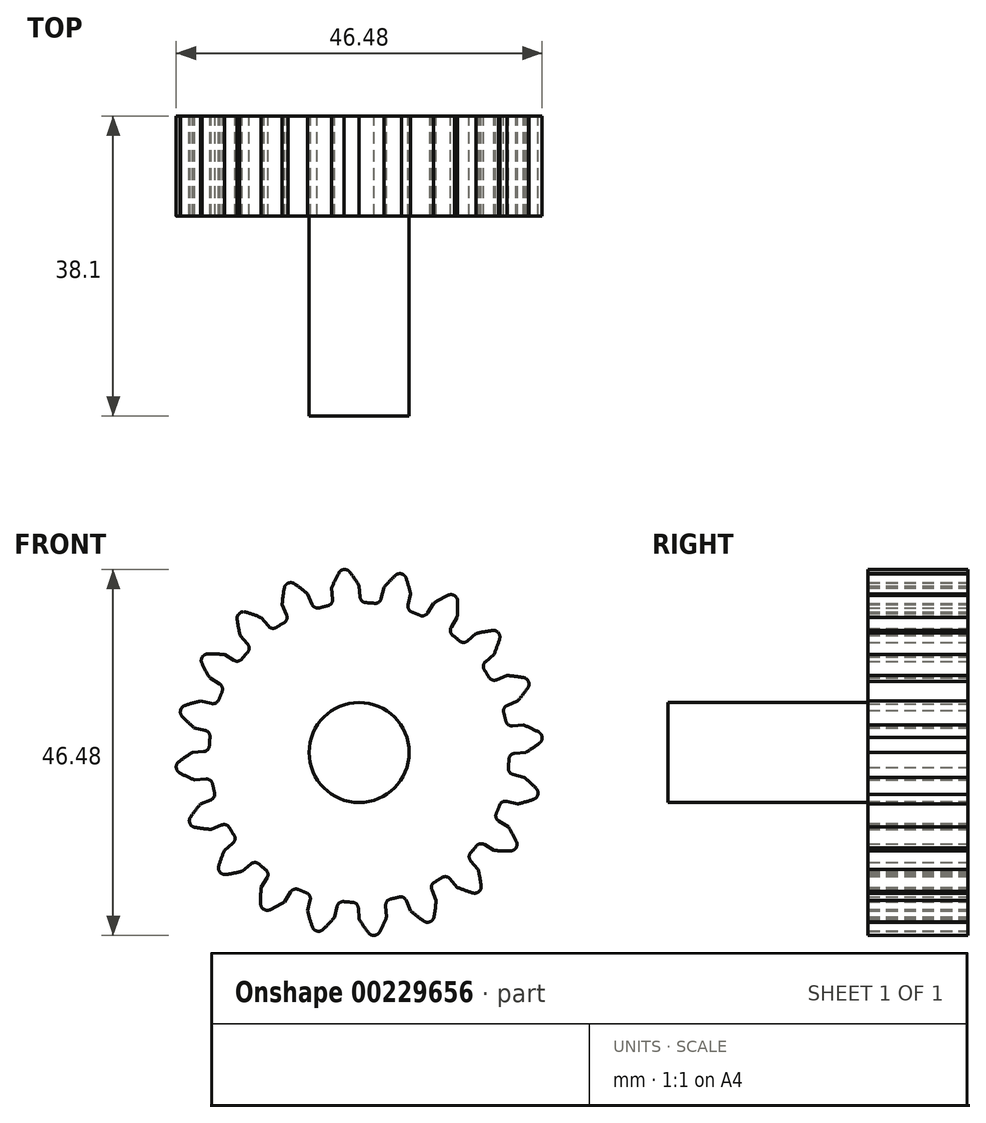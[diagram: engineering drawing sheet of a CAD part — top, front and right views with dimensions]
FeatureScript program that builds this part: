
annotation { "Feature Type Name" : "Feature", "Feature Type Description" : "" }
export const myFeature = defineFeature(function(context is Context, id is Id, definition is map)
    precondition{}
    {
        {
            var Q0;
            Q0=qCreatedBy(makeId("Front.planeOp"),FACE);
            var sketch = newSketch(context, id + "F0", { "sketchPlane" : qUnion([Q0])});
            skArc(sketch, "E0", {"start": v(-4, 18.63) * mm, "mid": v(-12.3, -14.54) * mm, "end": v(19.03, -0.86) * mm});
            skArc(sketch, "E1.trimOffspring", {"start": v(0, 21.17) * mm, "mid": v(-0.57, 22.06) * mm, "end": v(-1.2, 22.93) * mm});
            skLineSegment(sketch, "E2", {"start": v(-1.82, 23.24) * mm, "end": v(-1.92, 23.24) * mm});
            skLineSegment(sketch, "E3", {"start": v(0, 21.17) * mm, "end": v(0.11, 19.76) * mm});
            skLineSegment(sketch, "E4.MirrorCS", {"start": v(-2.01, 23.22) * mm, "end": v(-1.92, 23.24) * mm});
            skArc(sketch, "E5.MirrorCS", {"start": v(-3.49, 20.9) * mm, "mid": v(-3.06, 21.87) * mm, "end": v(-2.58, 22.82) * mm});
            skLineSegment(sketch, "E6.MirrorCS", {"start": v(-3.49, 20.9) * mm, "end": v(-3.38, 19.46) * mm});
            skPoint(sketch, "E7.visualSharp", {"position": v(0.17, 19.05) * mm});
            skArc(sketch, "E7.filletArc", {"start": v(0.11, 19.76) * mm, "mid": v(0.35, 19.25) * mm, "end": v(0.86, 19.03) * mm});
            skPoint(sketch, "E8.visualSharp", {"position": v(-3.32, 18.76) * mm});
            skArc(sketch, "E8.filletArc", {"start": v(-4, 18.63) * mm, "mid": v(-3.53, 18.93) * mm, "end": v(-3.38, 19.46) * mm});
            skPoint(sketch, "E9.visualSharp", {"position": v(-2.39, 23.16) * mm});
            skArc(sketch, "E9.filletArc", {"start": v(-2.01, 23.22) * mm, "mid": v(-2.34, 23.09) * mm, "end": v(-2.58, 22.82) * mm});
            skPoint(sketch, "E10.visualSharp", {"position": v(-1.44, 23.24) * mm});
            skArc(sketch, "E10.filletArc", {"start": v(-1.2, 22.93) * mm, "mid": v(-1.47, 23.16) * mm, "end": v(-1.82, 23.24) * mm});
            skArc(sketch, "E11.1.0", {"start": v(-9.56, 16.48) * mm, "mid": v(-9.2, 16.9) * mm, "end": v(-9.22, 17.46) * mm});
            skLineSegment(sketch, "E11.1.1", {"start": v(-9.77, 18.8) * mm, "end": v(-9.22, 17.46) * mm});
            skArc(sketch, "E11.1.2", {"start": v(-9.77, 18.8) * mm, "mid": v(-9.67, 19.85) * mm, "end": v(-9.5, 20.9) * mm});
            skArc(sketch, "E11.1.3", {"start": v(-9.09, 21.47) * mm, "mid": v(-9.36, 21.24) * mm, "end": v(-9.5, 20.9) * mm});
            skLineSegment(sketch, "E11.1.4", {"start": v(-9.09, 21.47) * mm, "end": v(-9, 21.5) * mm});
            skLineSegment(sketch, "E11.1.5", {"start": v(-8.92, 21.54) * mm, "end": v(-9, 21.5) * mm});
            skArc(sketch, "E11.1.6", {"start": v(-8.23, 21.44) * mm, "mid": v(-8.56, 21.57) * mm, "end": v(-8.92, 21.54) * mm});
            skArc(sketch, "E11.1.7", {"start": v(-6.54, 20.13) * mm, "mid": v(-7.36, 20.8) * mm, "end": v(-8.23, 21.44) * mm});
            skLineSegment(sketch, "E11.1.8", {"start": v(-6.54, 20.13) * mm, "end": v(-6, 18.82) * mm});
            skArc(sketch, "E11.1.9", {"start": v(-6, 18.82) * mm, "mid": v(-5.62, 18.42) * mm, "end": v(-5.06, 18.37) * mm});
            skArc(sketch, "E11.2.0", {"start": v(-14.18, 12.72) * mm, "mid": v(-13.98, 13.24) * mm, "end": v(-14.17, 13.76) * mm});
            skLineSegment(sketch, "E11.2.1", {"start": v(-15.1, 14.85) * mm, "end": v(-14.17, 13.76) * mm});
            skArc(sketch, "E11.2.2", {"start": v(-15.1, 14.85) * mm, "mid": v(-15.33, 15.9) * mm, "end": v(-15.5, 16.95) * mm});
            skArc(sketch, "E11.2.3", {"start": v(-15.28, 17.6) * mm, "mid": v(-15.47, 17.3) * mm, "end": v(-15.5, 16.95) * mm});
            skLineSegment(sketch, "E11.2.4", {"start": v(-15.28, 17.6) * mm, "end": v(-15.21, 17.67) * mm});
            skLineSegment(sketch, "E11.2.5", {"start": v(-15.13, 17.73) * mm, "end": v(-15.21, 17.67) * mm});
            skArc(sketch, "E11.2.6", {"start": v(-14.45, 17.85) * mm, "mid": v(-14.8, 17.87) * mm, "end": v(-15.13, 17.73) * mm});
            skArc(sketch, "E11.2.7", {"start": v(-12.44, 17.12) * mm, "mid": v(-13.43, 17.51) * mm, "end": v(-14.45, 17.85) * mm});
            skLineSegment(sketch, "E11.2.8", {"start": v(-12.44, 17.12) * mm, "end": v(-11.52, 16.05) * mm});
            skArc(sketch, "E11.2.9", {"start": v(-11.52, 16.05) * mm, "mid": v(-11.03, 15.78) * mm, "end": v(-10.49, 15.9) * mm});
            skArc(sketch, "E11.3.0", {"start": v(-17.42, 7.72) * mm, "mid": v(-17.39, 8.27) * mm, "end": v(-17.73, 8.7) * mm});
            skLineSegment(sketch, "E11.3.1", {"start": v(-18.95, 9.46) * mm, "end": v(-17.73, 8.7) * mm});
            skArc(sketch, "E11.3.2", {"start": v(-18.95, 9.46) * mm, "mid": v(-19.5, 10.38) * mm, "end": v(-19.98, 11.33) * mm});
            skArc(sketch, "E11.3.3", {"start": v(-19.97, 12.02) * mm, "mid": v(-20.06, 11.68) * mm, "end": v(-19.98, 11.33) * mm});
            skLineSegment(sketch, "E11.3.4", {"start": v(-19.97, 12.02) * mm, "end": v(-19.93, 12.1) * mm});
            skLineSegment(sketch, "E11.3.5", {"start": v(-19.87, 12.18) * mm, "end": v(-19.93, 12.1) * mm});
            skArc(sketch, "E11.3.6", {"start": v(-19.25, 12.5) * mm, "mid": v(-19.6, 12.42) * mm, "end": v(-19.87, 12.18) * mm});
            skArc(sketch, "E11.3.7", {"start": v(-17.12, 12.44) * mm, "mid": v(-18.19, 12.5) * mm, "end": v(-19.25, 12.5) * mm});
            skLineSegment(sketch, "E11.3.8", {"start": v(-17.12, 12.44) * mm, "end": v(-15.92, 11.7) * mm});
            skArc(sketch, "E11.3.9", {"start": v(-15.92, 11.7) * mm, "mid": v(-15.37, 11.6) * mm, "end": v(-14.9, 11.88) * mm});
            skArc(sketch, "E11.4.0", {"start": v(-18.95, 1.96) * mm, "mid": v(-19.09, 2.5) * mm, "end": v(-19.55, 2.8) * mm});
            skLineSegment(sketch, "E11.4.1", {"start": v(-20.95, 3.14) * mm, "end": v(-19.55, 2.8) * mm});
            skArc(sketch, "E11.4.2", {"start": v(-20.95, 3.14) * mm, "mid": v(-21.74, 3.85) * mm, "end": v(-22.5, 4.6) * mm});
            skArc(sketch, "E11.4.3", {"start": v(-22.7, 5.26) * mm, "mid": v(-22.68, 4.9) * mm, "end": v(-22.5, 4.6) * mm});
            skLineSegment(sketch, "E11.4.4", {"start": v(-22.7, 5.26) * mm, "end": v(-22.7, 5.36) * mm});
            skLineSegment(sketch, "E11.4.5", {"start": v(-22.66, 5.45) * mm, "end": v(-22.7, 5.36) * mm});
            skArc(sketch, "E11.4.6", {"start": v(-22.18, 5.95) * mm, "mid": v(-22.48, 5.75) * mm, "end": v(-22.66, 5.45) * mm});
            skArc(sketch, "E11.4.7", {"start": v(-20.13, 6.54) * mm, "mid": v(-21.16, 6.27) * mm, "end": v(-22.18, 5.95) * mm});
            skLineSegment(sketch, "E11.4.8", {"start": v(-20.13, 6.54) * mm, "end": v(-18.75, 6.21) * mm});
            skArc(sketch, "E11.4.9", {"start": v(-18.75, 6.21) * mm, "mid": v(-18.2, 6.28) * mm, "end": v(-17.83, 6.7) * mm});
            skArc(sketch, "E11.5.0", {"start": v(-18.63, -4) * mm, "mid": v(-18.93, -3.53) * mm, "end": v(-19.46, -3.38) * mm});
            skLineSegment(sketch, "E11.5.1", {"start": v(-20.9, -3.49) * mm, "end": v(-19.46, -3.38) * mm});
            skArc(sketch, "E11.5.2", {"start": v(-20.9, -3.49) * mm, "mid": v(-21.87, -3.06) * mm, "end": v(-22.82, -2.58) * mm});
            skArc(sketch, "E11.5.3", {"start": v(-23.22, -2.01) * mm, "mid": v(-23.09, -2.34) * mm, "end": v(-22.82, -2.58) * mm});
            skLineSegment(sketch, "E11.5.4", {"start": v(-23.22, -2.01) * mm, "end": v(-23.24, -1.92) * mm});
            skLineSegment(sketch, "E11.5.5", {"start": v(-23.24, -1.82) * mm, "end": v(-23.24, -1.92) * mm});
            skArc(sketch, "E11.5.6", {"start": v(-22.93, -1.2) * mm, "mid": v(-23.16, -1.47) * mm, "end": v(-23.24, -1.82) * mm});
            skArc(sketch, "E11.5.7", {"start": v(-21.17, 0) * mm, "mid": v(-22.06, -0.57) * mm, "end": v(-22.93, -1.2) * mm});
            skLineSegment(sketch, "E11.5.8", {"start": v(-21.17, 0) * mm, "end": v(-19.76, 0.11) * mm});
            skArc(sketch, "E11.5.9", {"start": v(-19.76, 0.11) * mm, "mid": v(-19.25, 0.35) * mm, "end": v(-19.03, 0.86) * mm});
            skArc(sketch, "E11.6.0", {"start": v(-16.48, -9.56) * mm, "mid": v(-16.9, -9.2) * mm, "end": v(-17.46, -9.22) * mm});
            skLineSegment(sketch, "E11.6.1", {"start": v(-18.8, -9.77) * mm, "end": v(-17.46, -9.22) * mm});
            skArc(sketch, "E11.6.2", {"start": v(-18.8, -9.77) * mm, "mid": v(-19.85, -9.67) * mm, "end": v(-20.9, -9.5) * mm});
            skArc(sketch, "E11.6.3", {"start": v(-21.47, -9.09) * mm, "mid": v(-21.24, -9.36) * mm, "end": v(-20.9, -9.5) * mm});
            skLineSegment(sketch, "E11.6.4", {"start": v(-21.47, -9.09) * mm, "end": v(-21.5, -9) * mm});
            skLineSegment(sketch, "E11.6.5", {"start": v(-21.54, -8.92) * mm, "end": v(-21.5, -9) * mm});
            skArc(sketch, "E11.6.6", {"start": v(-21.44, -8.23) * mm, "mid": v(-21.57, -8.56) * mm, "end": v(-21.54, -8.92) * mm});
            skArc(sketch, "E11.6.7", {"start": v(-20.13, -6.54) * mm, "mid": v(-20.8, -7.36) * mm, "end": v(-21.44, -8.23) * mm});
            skLineSegment(sketch, "E11.6.8", {"start": v(-20.13, -6.54) * mm, "end": v(-18.82, -6) * mm});
            skArc(sketch, "E11.6.9", {"start": v(-18.82, -6) * mm, "mid": v(-18.42, -5.62) * mm, "end": v(-18.37, -5.06) * mm});
            skArc(sketch, "E11.7.0", {"start": v(-12.72, -14.18) * mm, "mid": v(-13.24, -13.98) * mm, "end": v(-13.76, -14.17) * mm});
            skLineSegment(sketch, "E11.7.1", {"start": v(-14.85, -15.1) * mm, "end": v(-13.76, -14.17) * mm});
            skArc(sketch, "E11.7.2", {"start": v(-14.85, -15.1) * mm, "mid": v(-15.9, -15.33) * mm, "end": v(-16.95, -15.5) * mm});
            skArc(sketch, "E11.7.3", {"start": v(-17.6, -15.28) * mm, "mid": v(-17.3, -15.47) * mm, "end": v(-16.95, -15.5) * mm});
            skLineSegment(sketch, "E11.7.4", {"start": v(-17.6, -15.28) * mm, "end": v(-17.67, -15.21) * mm});
            skLineSegment(sketch, "E11.7.5", {"start": v(-17.73, -15.13) * mm, "end": v(-17.67, -15.21) * mm});
            skArc(sketch, "E11.7.6", {"start": v(-17.85, -14.45) * mm, "mid": v(-17.87, -14.8) * mm, "end": v(-17.73, -15.13) * mm});
            skArc(sketch, "E11.7.7", {"start": v(-17.12, -12.44) * mm, "mid": v(-17.51, -13.43) * mm, "end": v(-17.85, -14.45) * mm});
            skLineSegment(sketch, "E11.7.8", {"start": v(-17.12, -12.44) * mm, "end": v(-16.05, -11.52) * mm});
            skArc(sketch, "E11.7.9", {"start": v(-16.05, -11.52) * mm, "mid": v(-15.78, -11.03) * mm, "end": v(-15.9, -10.49) * mm});
            skArc(sketch, "E11.8.0", {"start": v(-7.72, -17.42) * mm, "mid": v(-8.27, -17.39) * mm, "end": v(-8.7, -17.73) * mm});
            skLineSegment(sketch, "E11.8.1", {"start": v(-9.46, -18.95) * mm, "end": v(-8.7, -17.73) * mm});
            skArc(sketch, "E11.8.2", {"start": v(-9.46, -18.95) * mm, "mid": v(-10.38, -19.5) * mm, "end": v(-11.33, -19.98) * mm});
            skArc(sketch, "E11.8.3", {"start": v(-12.02, -19.97) * mm, "mid": v(-11.68, -20.06) * mm, "end": v(-11.33, -19.98) * mm});
            skLineSegment(sketch, "E11.8.4", {"start": v(-12.02, -19.97) * mm, "end": v(-12.1, -19.93) * mm});
            skLineSegment(sketch, "E11.8.5", {"start": v(-12.18, -19.87) * mm, "end": v(-12.1, -19.93) * mm});
            skArc(sketch, "E11.8.6", {"start": v(-12.5, -19.25) * mm, "mid": v(-12.42, -19.6) * mm, "end": v(-12.18, -19.87) * mm});
            skArc(sketch, "E11.8.7", {"start": v(-12.44, -17.12) * mm, "mid": v(-12.5, -18.19) * mm, "end": v(-12.5, -19.25) * mm});
            skLineSegment(sketch, "E11.8.8", {"start": v(-12.44, -17.12) * mm, "end": v(-11.7, -15.92) * mm});
            skArc(sketch, "E11.8.9", {"start": v(-11.7, -15.92) * mm, "mid": v(-11.6, -15.37) * mm, "end": v(-11.88, -14.9) * mm});
            skArc(sketch, "E11.9.0", {"start": v(-1.96, -18.95) * mm, "mid": v(-2.5, -19.09) * mm, "end": v(-2.8, -19.55) * mm});
            skLineSegment(sketch, "E11.9.1", {"start": v(-3.14, -20.95) * mm, "end": v(-2.8, -19.55) * mm});
            skArc(sketch, "E11.9.2", {"start": v(-3.14, -20.95) * mm, "mid": v(-3.85, -21.74) * mm, "end": v(-4.6, -22.5) * mm});
            skArc(sketch, "E11.9.3", {"start": v(-5.26, -22.7) * mm, "mid": v(-4.9, -22.68) * mm, "end": v(-4.6, -22.5) * mm});
            skLineSegment(sketch, "E11.9.4", {"start": v(-5.26, -22.7) * mm, "end": v(-5.36, -22.7) * mm});
            skLineSegment(sketch, "E11.9.5", {"start": v(-5.45, -22.66) * mm, "end": v(-5.36, -22.7) * mm});
            skArc(sketch, "E11.9.6", {"start": v(-5.95, -22.18) * mm, "mid": v(-5.75, -22.48) * mm, "end": v(-5.45, -22.66) * mm});
            skArc(sketch, "E11.9.7", {"start": v(-6.54, -20.13) * mm, "mid": v(-6.27, -21.16) * mm, "end": v(-5.95, -22.18) * mm});
            skLineSegment(sketch, "E11.9.8", {"start": v(-6.54, -20.13) * mm, "end": v(-6.21, -18.75) * mm});
            skArc(sketch, "E11.9.9", {"start": v(-6.21, -18.75) * mm, "mid": v(-6.28, -18.2) * mm, "end": v(-6.7, -17.83) * mm});
            skArc(sketch, "E11.10.0", {"start": v(4, -18.63) * mm, "mid": v(3.53, -18.93) * mm, "end": v(3.38, -19.46) * mm});
            skLineSegment(sketch, "E11.10.1", {"start": v(3.49, -20.9) * mm, "end": v(3.38, -19.46) * mm});
            skArc(sketch, "E11.10.2", {"start": v(3.49, -20.9) * mm, "mid": v(3.06, -21.87) * mm, "end": v(2.58, -22.82) * mm});
            skArc(sketch, "E11.10.3", {"start": v(2.01, -23.22) * mm, "mid": v(2.34, -23.09) * mm, "end": v(2.58, -22.82) * mm});
            skLineSegment(sketch, "E11.10.4", {"start": v(2.01, -23.22) * mm, "end": v(1.92, -23.24) * mm});
            skLineSegment(sketch, "E11.10.5", {"start": v(1.82, -23.24) * mm, "end": v(1.92, -23.24) * mm});
            skArc(sketch, "E11.10.6", {"start": v(1.2, -22.93) * mm, "mid": v(1.47, -23.16) * mm, "end": v(1.82, -23.24) * mm});
            skArc(sketch, "E11.10.7", {"start": v(0, -21.17) * mm, "mid": v(0.57, -22.06) * mm, "end": v(1.2, -22.93) * mm});
            skLineSegment(sketch, "E11.10.8", {"start": v(0, -21.17) * mm, "end": v(-0.11, -19.76) * mm});
            skArc(sketch, "E11.10.9", {"start": v(-0.11, -19.76) * mm, "mid": v(-0.35, -19.25) * mm, "end": v(-0.86, -19.03) * mm});
            skArc(sketch, "E11.11.0", {"start": v(9.56, -16.48) * mm, "mid": v(9.2, -16.9) * mm, "end": v(9.22, -17.46) * mm});
            skLineSegment(sketch, "E11.11.1", {"start": v(9.77, -18.8) * mm, "end": v(9.22, -17.46) * mm});
            skArc(sketch, "E11.11.2", {"start": v(9.77, -18.8) * mm, "mid": v(9.67, -19.85) * mm, "end": v(9.5, -20.9) * mm});
            skArc(sketch, "E11.11.3", {"start": v(9.09, -21.47) * mm, "mid": v(9.36, -21.24) * mm, "end": v(9.5, -20.9) * mm});
            skLineSegment(sketch, "E11.11.4", {"start": v(9.09, -21.47) * mm, "end": v(9, -21.5) * mm});
            skLineSegment(sketch, "E11.11.5", {"start": v(8.92, -21.54) * mm, "end": v(9, -21.5) * mm});
            skArc(sketch, "E11.11.6", {"start": v(8.23, -21.44) * mm, "mid": v(8.56, -21.57) * mm, "end": v(8.92, -21.54) * mm});
            skArc(sketch, "E11.11.7", {"start": v(6.54, -20.13) * mm, "mid": v(7.36, -20.8) * mm, "end": v(8.23, -21.44) * mm});
            skLineSegment(sketch, "E11.11.8", {"start": v(6.54, -20.13) * mm, "end": v(6, -18.82) * mm});
            skArc(sketch, "E11.11.9", {"start": v(6, -18.82) * mm, "mid": v(5.62, -18.42) * mm, "end": v(5.06, -18.37) * mm});
            skArc(sketch, "E11.12.0", {"start": v(14.18, -12.72) * mm, "mid": v(13.98, -13.24) * mm, "end": v(14.17, -13.76) * mm});
            skLineSegment(sketch, "E11.12.1", {"start": v(15.1, -14.85) * mm, "end": v(14.17, -13.76) * mm});
            skArc(sketch, "E11.12.2", {"start": v(15.1, -14.85) * mm, "mid": v(15.33, -15.9) * mm, "end": v(15.5, -16.95) * mm});
            skArc(sketch, "E11.12.3", {"start": v(15.28, -17.6) * mm, "mid": v(15.47, -17.3) * mm, "end": v(15.5, -16.95) * mm});
            skLineSegment(sketch, "E11.12.4", {"start": v(15.28, -17.6) * mm, "end": v(15.21, -17.67) * mm});
            skLineSegment(sketch, "E11.12.5", {"start": v(15.13, -17.73) * mm, "end": v(15.21, -17.67) * mm});
            skArc(sketch, "E11.12.6", {"start": v(14.45, -17.85) * mm, "mid": v(14.8, -17.87) * mm, "end": v(15.13, -17.73) * mm});
            skArc(sketch, "E11.12.7", {"start": v(12.44, -17.12) * mm, "mid": v(13.43, -17.51) * mm, "end": v(14.45, -17.85) * mm});
            skLineSegment(sketch, "E11.12.8", {"start": v(12.44, -17.12) * mm, "end": v(11.52, -16.05) * mm});
            skArc(sketch, "E11.12.9", {"start": v(11.52, -16.05) * mm, "mid": v(11.03, -15.78) * mm, "end": v(10.49, -15.9) * mm});
            skArc(sketch, "E11.13.0", {"start": v(17.42, -7.72) * mm, "mid": v(17.39, -8.27) * mm, "end": v(17.73, -8.7) * mm});
            skLineSegment(sketch, "E11.13.1", {"start": v(18.95, -9.46) * mm, "end": v(17.73, -8.7) * mm});
            skArc(sketch, "E11.13.2", {"start": v(18.95, -9.46) * mm, "mid": v(19.5, -10.38) * mm, "end": v(19.98, -11.33) * mm});
            skArc(sketch, "E11.13.3", {"start": v(19.97, -12.02) * mm, "mid": v(20.06, -11.68) * mm, "end": v(19.98, -11.33) * mm});
            skLineSegment(sketch, "E11.13.4", {"start": v(19.97, -12.02) * mm, "end": v(19.93, -12.1) * mm});
            skLineSegment(sketch, "E11.13.5", {"start": v(19.87, -12.18) * mm, "end": v(19.93, -12.1) * mm});
            skArc(sketch, "E11.13.6", {"start": v(19.25, -12.5) * mm, "mid": v(19.6, -12.42) * mm, "end": v(19.87, -12.18) * mm});
            skArc(sketch, "E11.13.7", {"start": v(17.12, -12.44) * mm, "mid": v(18.19, -12.5) * mm, "end": v(19.25, -12.5) * mm});
            skLineSegment(sketch, "E11.13.8", {"start": v(17.12, -12.44) * mm, "end": v(15.92, -11.7) * mm});
            skArc(sketch, "E11.13.9", {"start": v(15.92, -11.7) * mm, "mid": v(15.37, -11.6) * mm, "end": v(14.9, -11.88) * mm});
            skArc(sketch, "E11.14.0", {"start": v(18.95, -1.96) * mm, "mid": v(19.09, -2.5) * mm, "end": v(19.55, -2.8) * mm});
            skLineSegment(sketch, "E11.14.1", {"start": v(20.95, -3.14) * mm, "end": v(19.55, -2.8) * mm});
            skArc(sketch, "E11.14.2", {"start": v(20.95, -3.14) * mm, "mid": v(21.74, -3.85) * mm, "end": v(22.5, -4.6) * mm});
            skArc(sketch, "E11.14.3", {"start": v(22.7, -5.26) * mm, "mid": v(22.68, -4.9) * mm, "end": v(22.5, -4.6) * mm});
            skLineSegment(sketch, "E11.14.4", {"start": v(22.7, -5.26) * mm, "end": v(22.7, -5.36) * mm});
            skLineSegment(sketch, "E11.14.5", {"start": v(22.66, -5.45) * mm, "end": v(22.7, -5.36) * mm});
            skArc(sketch, "E11.14.6", {"start": v(22.18, -5.95) * mm, "mid": v(22.48, -5.75) * mm, "end": v(22.66, -5.45) * mm});
            skArc(sketch, "E11.14.7", {"start": v(20.13, -6.54) * mm, "mid": v(21.16, -6.27) * mm, "end": v(22.18, -5.95) * mm});
            skLineSegment(sketch, "E11.14.8", {"start": v(20.13, -6.54) * mm, "end": v(18.75, -6.21) * mm});
            skArc(sketch, "E11.14.9", {"start": v(18.75, -6.21) * mm, "mid": v(18.2, -6.28) * mm, "end": v(17.83, -6.7) * mm});
            skArc(sketch, "E11.15.0", {"start": v(18.63, 4) * mm, "mid": v(18.93, 3.53) * mm, "end": v(19.46, 3.38) * mm});
            skLineSegment(sketch, "E11.15.1", {"start": v(20.9, 3.49) * mm, "end": v(19.46, 3.38) * mm});
            skArc(sketch, "E11.15.2", {"start": v(20.9, 3.49) * mm, "mid": v(21.87, 3.06) * mm, "end": v(22.82, 2.58) * mm});
            skArc(sketch, "E11.15.3", {"start": v(23.22, 2.01) * mm, "mid": v(23.09, 2.34) * mm, "end": v(22.82, 2.58) * mm});
            skLineSegment(sketch, "E11.15.4", {"start": v(23.22, 2.01) * mm, "end": v(23.24, 1.92) * mm});
            skLineSegment(sketch, "E11.15.5", {"start": v(23.24, 1.82) * mm, "end": v(23.24, 1.92) * mm});
            skArc(sketch, "E11.15.6", {"start": v(22.93, 1.2) * mm, "mid": v(23.16, 1.47) * mm, "end": v(23.24, 1.82) * mm});
            skArc(sketch, "E11.15.7", {"start": v(21.17, 0) * mm, "mid": v(22.06, 0.57) * mm, "end": v(22.93, 1.2) * mm});
            skLineSegment(sketch, "E11.15.8", {"start": v(21.17, 0) * mm, "end": v(19.76, -0.11) * mm});
            skArc(sketch, "E11.15.9", {"start": v(19.76, -0.11) * mm, "mid": v(19.25, -0.35) * mm, "end": v(19.03, -0.86) * mm});
            skArc(sketch, "E11.16.0", {"start": v(16.48, 9.56) * mm, "mid": v(16.9, 9.2) * mm, "end": v(17.46, 9.22) * mm});
            skLineSegment(sketch, "E11.16.1", {"start": v(18.8, 9.77) * mm, "end": v(17.46, 9.22) * mm});
            skArc(sketch, "E11.16.2", {"start": v(18.8, 9.77) * mm, "mid": v(19.85, 9.67) * mm, "end": v(20.9, 9.5) * mm});
            skArc(sketch, "E11.16.3", {"start": v(21.47, 9.09) * mm, "mid": v(21.24, 9.36) * mm, "end": v(20.9, 9.5) * mm});
            skLineSegment(sketch, "E11.16.4", {"start": v(21.47, 9.09) * mm, "end": v(21.5, 9) * mm});
            skLineSegment(sketch, "E11.16.5", {"start": v(21.54, 8.92) * mm, "end": v(21.5, 9) * mm});
            skArc(sketch, "E11.16.6", {"start": v(21.44, 8.23) * mm, "mid": v(21.57, 8.56) * mm, "end": v(21.54, 8.92) * mm});
            skArc(sketch, "E11.16.7", {"start": v(20.13, 6.54) * mm, "mid": v(20.8, 7.36) * mm, "end": v(21.44, 8.23) * mm});
            skLineSegment(sketch, "E11.16.8", {"start": v(20.13, 6.54) * mm, "end": v(18.82, 6) * mm});
            skArc(sketch, "E11.16.9", {"start": v(18.82, 6) * mm, "mid": v(18.42, 5.62) * mm, "end": v(18.37, 5.06) * mm});
            skArc(sketch, "E11.17.0", {"start": v(12.72, 14.18) * mm, "mid": v(13.24, 13.98) * mm, "end": v(13.76, 14.17) * mm});
            skLineSegment(sketch, "E11.17.1", {"start": v(14.85, 15.1) * mm, "end": v(13.76, 14.17) * mm});
            skArc(sketch, "E11.17.2", {"start": v(14.85, 15.1) * mm, "mid": v(15.9, 15.33) * mm, "end": v(16.95, 15.5) * mm});
            skArc(sketch, "E11.17.3", {"start": v(17.6, 15.28) * mm, "mid": v(17.3, 15.47) * mm, "end": v(16.95, 15.5) * mm});
            skLineSegment(sketch, "E11.17.4", {"start": v(17.6, 15.28) * mm, "end": v(17.67, 15.21) * mm});
            skLineSegment(sketch, "E11.17.5", {"start": v(17.73, 15.13) * mm, "end": v(17.67, 15.21) * mm});
            skArc(sketch, "E11.17.6", {"start": v(17.85, 14.45) * mm, "mid": v(17.87, 14.8) * mm, "end": v(17.73, 15.13) * mm});
            skArc(sketch, "E11.17.7", {"start": v(17.12, 12.44) * mm, "mid": v(17.51, 13.43) * mm, "end": v(17.85, 14.45) * mm});
            skLineSegment(sketch, "E11.17.8", {"start": v(17.12, 12.44) * mm, "end": v(16.05, 11.52) * mm});
            skArc(sketch, "E11.17.9", {"start": v(16.05, 11.52) * mm, "mid": v(15.78, 11.03) * mm, "end": v(15.9, 10.49) * mm});
            skArc(sketch, "E11.18.0", {"start": v(7.72, 17.42) * mm, "mid": v(8.27, 17.39) * mm, "end": v(8.7, 17.73) * mm});
            skLineSegment(sketch, "E11.18.1", {"start": v(9.46, 18.95) * mm, "end": v(8.7, 17.73) * mm});
            skArc(sketch, "E11.18.2", {"start": v(9.46, 18.95) * mm, "mid": v(10.38, 19.5) * mm, "end": v(11.33, 19.98) * mm});
            skArc(sketch, "E11.18.3", {"start": v(12.02, 19.97) * mm, "mid": v(11.68, 20.06) * mm, "end": v(11.33, 19.98) * mm});
            skLineSegment(sketch, "E11.18.4", {"start": v(12.02, 19.97) * mm, "end": v(12.1, 19.93) * mm});
            skLineSegment(sketch, "E11.18.5", {"start": v(12.18, 19.87) * mm, "end": v(12.1, 19.93) * mm});
            skArc(sketch, "E11.18.6", {"start": v(12.5, 19.25) * mm, "mid": v(12.42, 19.6) * mm, "end": v(12.18, 19.87) * mm});
            skArc(sketch, "E11.18.7", {"start": v(12.44, 17.12) * mm, "mid": v(12.5, 18.19) * mm, "end": v(12.5, 19.25) * mm});
            skLineSegment(sketch, "E11.18.8", {"start": v(12.44, 17.12) * mm, "end": v(11.7, 15.92) * mm});
            skArc(sketch, "E11.18.9", {"start": v(11.7, 15.92) * mm, "mid": v(11.6, 15.37) * mm, "end": v(11.88, 14.9) * mm});
            skArc(sketch, "E11.19.0", {"start": v(1.96, 18.95) * mm, "mid": v(2.5, 19.09) * mm, "end": v(2.8, 19.55) * mm});
            skLineSegment(sketch, "E11.19.1", {"start": v(3.14, 20.95) * mm, "end": v(2.8, 19.55) * mm});
            skArc(sketch, "E11.19.2", {"start": v(3.14, 20.95) * mm, "mid": v(3.85, 21.74) * mm, "end": v(4.6, 22.5) * mm});
            skArc(sketch, "E11.19.3", {"start": v(5.26, 22.7) * mm, "mid": v(4.9, 22.68) * mm, "end": v(4.6, 22.5) * mm});
            skLineSegment(sketch, "E11.19.4", {"start": v(5.26, 22.7) * mm, "end": v(5.36, 22.7) * mm});
            skLineSegment(sketch, "E11.19.5", {"start": v(5.45, 22.66) * mm, "end": v(5.36, 22.7) * mm});
            skArc(sketch, "E11.19.6", {"start": v(5.95, 22.18) * mm, "mid": v(5.75, 22.48) * mm, "end": v(5.45, 22.66) * mm});
            skArc(sketch, "E11.19.7", {"start": v(6.54, 20.13) * mm, "mid": v(6.27, 21.16) * mm, "end": v(5.95, 22.18) * mm});
            skLineSegment(sketch, "E11.19.8", {"start": v(6.54, 20.13) * mm, "end": v(6.21, 18.75) * mm});
            skArc(sketch, "E11.19.9", {"start": v(6.21, 18.75) * mm, "mid": v(6.28, 18.2) * mm, "end": v(6.7, 17.83) * mm});
            skArc(sketch, "E12.trimOffspring", {"start": v(1.96, 18.95) * mm, "mid": v(1.4, 19) * mm, "end": v(0.86, 19.03) * mm});
            skArc(sketch, "E13.trimOffspring", {"start": v(7.72, 17.42) * mm, "mid": v(7.21, 17.63) * mm, "end": v(6.7, 17.83) * mm});
            skArc(sketch, "E14.trimOffspring", {"start": v(12.72, 14.18) * mm, "mid": v(12.3, 14.54) * mm, "end": v(11.88, 14.9) * mm});
            skArc(sketch, "E15.trimOffspring", {"start": v(16.48, 9.56) * mm, "mid": v(16.2, 10.03) * mm, "end": v(15.9, 10.49) * mm});
            skArc(sketch, "E16.trimOffspring", {"start": v(18.63, 4) * mm, "mid": v(18.5, 4.53) * mm, "end": v(18.37, 5.06) * mm});
            skSolve(sketch);
        }
        {
            var Q0;
            Q0=qSketchRegion(id+"F0",true);
            extrude(context, id + "F1", {"entities" : qUnion([Q0]), "depth" : 12.7 * mm});
        }
        {
            var Q0;
            Q0=makeQuery(id+"F1.opExtrude","CAP_FACE",FACE,{"disambiguationData":[OSD([sQuery(id+"F0.wireOp",EDGE,"E0"),sQuery(id+"F0.wireOp",EDGE,"E1.trimOffspring"),sQuery(id+"F0.wireOp",EDGE,"E2"),sQuery(id+"F0.wireOp",EDGE,"E3"),sQuery(id+"F0.wireOp",EDGE,"E4.MirrorCS"),sQuery(id+"F0.wireOp",EDGE,"E5.MirrorCS"),sQuery(id+"F0.wireOp",EDGE,"E6.MirrorCS"),sQuery(id+"F0.wireOp",EDGE,"E7.filletArc"),sQuery(id+"F0.wireOp",EDGE,"E8.filletArc"),sQuery(id+"F0.wireOp",EDGE,"E9.filletArc"),sQuery(id+"F0.wireOp",EDGE,"E10.filletArc"),sQuery(id+"F0.wireOp",EDGE,"E11.1.0"),sQuery(id+"F0.wireOp",EDGE,"E11.1.1"),sQuery(id+"F0.wireOp",EDGE,"E11.1.2"),sQuery(id+"F0.wireOp",EDGE,"E11.1.3"),sQuery(id+"F0.wireOp",EDGE,"E11.1.4"),sQuery(id+"F0.wireOp",EDGE,"E11.1.5"),sQuery(id+"F0.wireOp",EDGE,"E11.1.6"),sQuery(id+"F0.wireOp",EDGE,"E11.1.7"),sQuery(id+"F0.wireOp",EDGE,"E11.1.8"),sQuery(id+"F0.wireOp",EDGE,"E11.1.9"),sQuery(id+"F0.wireOp",EDGE,"E11.2.0"),sQuery(id+"F0.wireOp",EDGE,"E11.2.1"),sQuery(id+"F0.wireOp",EDGE,"E11.2.2"),sQuery(id+"F0.wireOp",EDGE,"E11.2.3"),sQuery(id+"F0.wireOp",EDGE,"E11.2.4"),sQuery(id+"F0.wireOp",EDGE,"E11.2.5"),sQuery(id+"F0.wireOp",EDGE,"E11.2.6"),sQuery(id+"F0.wireOp",EDGE,"E11.2.7"),sQuery(id+"F0.wireOp",EDGE,"E11.2.8"),sQuery(id+"F0.wireOp",EDGE,"E11.2.9"),sQuery(id+"F0.wireOp",EDGE,"E11.3.0"),sQuery(id+"F0.wireOp",EDGE,"E11.3.1"),sQuery(id+"F0.wireOp",EDGE,"E11.3.2"),sQuery(id+"F0.wireOp",EDGE,"E11.3.3"),sQuery(id+"F0.wireOp",EDGE,"E11.3.4"),sQuery(id+"F0.wireOp",EDGE,"E11.3.5"),sQuery(id+"F0.wireOp",EDGE,"E11.3.6"),sQuery(id+"F0.wireOp",EDGE,"E11.3.7"),sQuery(id+"F0.wireOp",EDGE,"E11.3.8"),sQuery(id+"F0.wireOp",EDGE,"E11.3.9"),sQuery(id+"F0.wireOp",EDGE,"E11.4.0"),sQuery(id+"F0.wireOp",EDGE,"E11.4.1"),sQuery(id+"F0.wireOp",EDGE,"E11.4.2"),sQuery(id+"F0.wireOp",EDGE,"E11.4.3"),sQuery(id+"F0.wireOp",EDGE,"E11.4.4"),sQuery(id+"F0.wireOp",EDGE,"E11.4.5"),sQuery(id+"F0.wireOp",EDGE,"E11.4.6"),sQuery(id+"F0.wireOp",EDGE,"E11.4.7"),sQuery(id+"F0.wireOp",EDGE,"E11.4.8"),sQuery(id+"F0.wireOp",EDGE,"E11.4.9"),sQuery(id+"F0.wireOp",EDGE,"E11.5.0"),sQuery(id+"F0.wireOp",EDGE,"E11.5.1"),sQuery(id+"F0.wireOp",EDGE,"E11.5.2"),sQuery(id+"F0.wireOp",EDGE,"E11.5.3"),sQuery(id+"F0.wireOp",EDGE,"E11.5.4"),sQuery(id+"F0.wireOp",EDGE,"E11.5.5"),sQuery(id+"F0.wireOp",EDGE,"E11.5.6"),sQuery(id+"F0.wireOp",EDGE,"E11.5.7"),sQuery(id+"F0.wireOp",EDGE,"E11.5.8"),sQuery(id+"F0.wireOp",EDGE,"E11.5.9"),sQuery(id+"F0.wireOp",EDGE,"E11.6.0"),sQuery(id+"F0.wireOp",EDGE,"E11.6.1"),sQuery(id+"F0.wireOp",EDGE,"E11.6.2"),sQuery(id+"F0.wireOp",EDGE,"E11.6.3"),sQuery(id+"F0.wireOp",EDGE,"E11.6.4"),sQuery(id+"F0.wireOp",EDGE,"E11.6.5"),sQuery(id+"F0.wireOp",EDGE,"E11.6.6"),sQuery(id+"F0.wireOp",EDGE,"E11.6.7"),sQuery(id+"F0.wireOp",EDGE,"E11.6.8"),sQuery(id+"F0.wireOp",EDGE,"E11.6.9"),sQuery(id+"F0.wireOp",EDGE,"E11.7.0"),sQuery(id+"F0.wireOp",EDGE,"E11.7.1"),sQuery(id+"F0.wireOp",EDGE,"E11.7.2"),sQuery(id+"F0.wireOp",EDGE,"E11.7.3"),sQuery(id+"F0.wireOp",EDGE,"E11.7.4"),sQuery(id+"F0.wireOp",EDGE,"E11.7.5"),sQuery(id+"F0.wireOp",EDGE,"E11.7.6"),sQuery(id+"F0.wireOp",EDGE,"E11.7.7"),sQuery(id+"F0.wireOp",EDGE,"E11.7.8"),sQuery(id+"F0.wireOp",EDGE,"E11.7.9"),sQuery(id+"F0.wireOp",EDGE,"E11.8.0"),sQuery(id+"F0.wireOp",EDGE,"E11.8.1"),sQuery(id+"F0.wireOp",EDGE,"E11.8.2"),sQuery(id+"F0.wireOp",EDGE,"E11.8.3"),sQuery(id+"F0.wireOp",EDGE,"E11.8.4"),sQuery(id+"F0.wireOp",EDGE,"E11.8.5"),sQuery(id+"F0.wireOp",EDGE,"E11.8.6"),sQuery(id+"F0.wireOp",EDGE,"E11.8.7"),sQuery(id+"F0.wireOp",EDGE,"E11.8.8"),sQuery(id+"F0.wireOp",EDGE,"E11.8.9"),sQuery(id+"F0.wireOp",EDGE,"E11.9.0"),sQuery(id+"F0.wireOp",EDGE,"E11.9.1"),sQuery(id+"F0.wireOp",EDGE,"E11.9.2"),sQuery(id+"F0.wireOp",EDGE,"E11.9.3"),sQuery(id+"F0.wireOp",EDGE,"E11.9.4"),sQuery(id+"F0.wireOp",EDGE,"E11.9.5"),sQuery(id+"F0.wireOp",EDGE,"E11.9.6"),sQuery(id+"F0.wireOp",EDGE,"E11.9.7"),sQuery(id+"F0.wireOp",EDGE,"E11.9.8"),sQuery(id+"F0.wireOp",EDGE,"E11.9.9"),sQuery(id+"F0.wireOp",EDGE,"E11.10.0"),sQuery(id+"F0.wireOp",EDGE,"E11.10.1"),sQuery(id+"F0.wireOp",EDGE,"E11.10.2"),sQuery(id+"F0.wireOp",EDGE,"E11.10.3"),sQuery(id+"F0.wireOp",EDGE,"E11.10.4"),sQuery(id+"F0.wireOp",EDGE,"E11.10.5"),sQuery(id+"F0.wireOp",EDGE,"E11.10.6"),sQuery(id+"F0.wireOp",EDGE,"E11.10.7"),sQuery(id+"F0.wireOp",EDGE,"E11.10.8"),sQuery(id+"F0.wireOp",EDGE,"E11.10.9"),sQuery(id+"F0.wireOp",EDGE,"E11.11.0"),sQuery(id+"F0.wireOp",EDGE,"E11.11.1"),sQuery(id+"F0.wireOp",EDGE,"E11.11.2"),sQuery(id+"F0.wireOp",EDGE,"E11.11.3"),sQuery(id+"F0.wireOp",EDGE,"E11.11.4"),sQuery(id+"F0.wireOp",EDGE,"E11.11.5"),sQuery(id+"F0.wireOp",EDGE,"E11.11.6"),sQuery(id+"F0.wireOp",EDGE,"E11.11.7"),sQuery(id+"F0.wireOp",EDGE,"E11.11.8"),sQuery(id+"F0.wireOp",EDGE,"E11.11.9"),sQuery(id+"F0.wireOp",EDGE,"E11.12.0"),sQuery(id+"F0.wireOp",EDGE,"E11.12.1"),sQuery(id+"F0.wireOp",EDGE,"E11.12.2"),sQuery(id+"F0.wireOp",EDGE,"E11.12.3"),sQuery(id+"F0.wireOp",EDGE,"E11.12.4"),sQuery(id+"F0.wireOp",EDGE,"E11.12.5"),sQuery(id+"F0.wireOp",EDGE,"E11.12.6"),sQuery(id+"F0.wireOp",EDGE,"E11.12.7"),sQuery(id+"F0.wireOp",EDGE,"E11.12.8"),sQuery(id+"F0.wireOp",EDGE,"E11.12.9"),sQuery(id+"F0.wireOp",EDGE,"E11.13.0"),sQuery(id+"F0.wireOp",EDGE,"E11.13.1"),sQuery(id+"F0.wireOp",EDGE,"E11.13.2"),sQuery(id+"F0.wireOp",EDGE,"E11.13.3"),sQuery(id+"F0.wireOp",EDGE,"E11.13.4"),sQuery(id+"F0.wireOp",EDGE,"E11.13.5"),sQuery(id+"F0.wireOp",EDGE,"E11.13.6"),sQuery(id+"F0.wireOp",EDGE,"E11.13.7"),sQuery(id+"F0.wireOp",EDGE,"E11.13.8"),sQuery(id+"F0.wireOp",EDGE,"E11.13.9"),sQuery(id+"F0.wireOp",EDGE,"E11.14.0"),sQuery(id+"F0.wireOp",EDGE,"E11.14.1"),sQuery(id+"F0.wireOp",EDGE,"E11.14.2"),sQuery(id+"F0.wireOp",EDGE,"E11.14.3"),sQuery(id+"F0.wireOp",EDGE,"E11.14.4"),sQuery(id+"F0.wireOp",EDGE,"E11.14.5"),sQuery(id+"F0.wireOp",EDGE,"E11.14.6"),sQuery(id+"F0.wireOp",EDGE,"E11.14.7"),sQuery(id+"F0.wireOp",EDGE,"E11.14.8"),sQuery(id+"F0.wireOp",EDGE,"E11.14.9"),sQuery(id+"F0.wireOp",EDGE,"E11.15.0"),sQuery(id+"F0.wireOp",EDGE,"E11.15.1"),sQuery(id+"F0.wireOp",EDGE,"E11.15.2"),sQuery(id+"F0.wireOp",EDGE,"E11.15.3"),sQuery(id+"F0.wireOp",EDGE,"E11.15.4"),sQuery(id+"F0.wireOp",EDGE,"E11.15.5"),sQuery(id+"F0.wireOp",EDGE,"E11.15.6"),sQuery(id+"F0.wireOp",EDGE,"E11.15.7"),sQuery(id+"F0.wireOp",EDGE,"E11.15.8"),sQuery(id+"F0.wireOp",EDGE,"E11.15.9"),sQuery(id+"F0.wireOp",EDGE,"E11.16.0"),sQuery(id+"F0.wireOp",EDGE,"E11.16.1"),sQuery(id+"F0.wireOp",EDGE,"E11.16.2"),sQuery(id+"F0.wireOp",EDGE,"E11.16.3"),sQuery(id+"F0.wireOp",EDGE,"E11.16.4"),sQuery(id+"F0.wireOp",EDGE,"E11.16.5"),sQuery(id+"F0.wireOp",EDGE,"E11.16.6"),sQuery(id+"F0.wireOp",EDGE,"E11.16.7"),sQuery(id+"F0.wireOp",EDGE,"E11.16.8"),sQuery(id+"F0.wireOp",EDGE,"E11.16.9"),sQuery(id+"F0.wireOp",EDGE,"E11.17.0"),sQuery(id+"F0.wireOp",EDGE,"E11.17.1"),sQuery(id+"F0.wireOp",EDGE,"E11.17.2"),sQuery(id+"F0.wireOp",EDGE,"E11.17.3"),sQuery(id+"F0.wireOp",EDGE,"E11.17.4"),sQuery(id+"F0.wireOp",EDGE,"E11.17.5"),sQuery(id+"F0.wireOp",EDGE,"E11.17.6"),sQuery(id+"F0.wireOp",EDGE,"E11.17.7"),sQuery(id+"F0.wireOp",EDGE,"E11.17.8"),sQuery(id+"F0.wireOp",EDGE,"E11.17.9"),sQuery(id+"F0.wireOp",EDGE,"E11.18.0"),sQuery(id+"F0.wireOp",EDGE,"E11.18.1"),sQuery(id+"F0.wireOp",EDGE,"E11.18.2"),sQuery(id+"F0.wireOp",EDGE,"E11.18.3"),sQuery(id+"F0.wireOp",EDGE,"E11.18.4"),sQuery(id+"F0.wireOp",EDGE,"E11.18.5"),sQuery(id+"F0.wireOp",EDGE,"E11.18.6"),sQuery(id+"F0.wireOp",EDGE,"E11.18.7"),sQuery(id+"F0.wireOp",EDGE,"E11.18.8"),sQuery(id+"F0.wireOp",EDGE,"E11.18.9"),sQuery(id+"F0.wireOp",EDGE,"E11.19.0"),sQuery(id+"F0.wireOp",EDGE,"E11.19.1"),sQuery(id+"F0.wireOp",EDGE,"E11.19.2"),sQuery(id+"F0.wireOp",EDGE,"E11.19.3"),sQuery(id+"F0.wireOp",EDGE,"E11.19.4"),sQuery(id+"F0.wireOp",EDGE,"E11.19.5"),sQuery(id+"F0.wireOp",EDGE,"E11.19.6"),sQuery(id+"F0.wireOp",EDGE,"E11.19.7"),sQuery(id+"F0.wireOp",EDGE,"E11.19.8"),sQuery(id+"F0.wireOp",EDGE,"E11.19.9"),sQuery(id+"F0.wireOp",EDGE,"E12.trimOffspring"),sQuery(id+"F0.wireOp",EDGE,"E13.trimOffspring"),sQuery(id+"F0.wireOp",EDGE,"E14.trimOffspring"),sQuery(id+"F0.wireOp",EDGE,"E15.trimOffspring"),sQuery(id+"F0.wireOp",EDGE,"E16.trimOffspring")])],"isStart":false});
            var sketch = newSketch(context, id + "F2", { "sketchPlane" : qUnion([Q0])});
            skCircle(sketch, "E17", {"center": v(0, 0) * mm, "radius": 6.35 * mm});
            skSolve(sketch);
        }
        {
            var Q0;
            Q0 = qSketchRegion(id + "F2", true);
            extrude(context, id + "F3", {"entities" : qUnion([Q0]), "operationType" : NewBodyOperationType.ADD, "depth" : 25.4 * mm});
        }
    });
